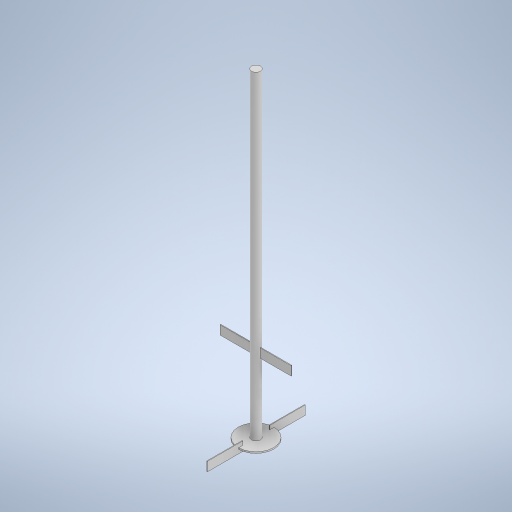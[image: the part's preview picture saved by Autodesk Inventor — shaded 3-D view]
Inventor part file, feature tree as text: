
AUTODESK INVENTOR PART (.ipt)
format: ipt  version: 2024 (Build 280153000, 153)  size: 284,160 bytes
history: native  units: mm
features: extrude x4, sketch x4
ambient origin geometry x8: Origin, YZ Plane, XZ Plane, XY Plane, X Axis, Y Axis, Z Axis, Center Point
bodies: Solid1 (feature_tree)
feature tree (8):
  extrude  "Extrusion1"  Depth=900.0mm TaperAngle=0.0deg
  extrude  "Extrusion2"  Depth=4.0mm TaperAngle=0.0deg
  extrude  "Extrusion3"  Depth=100.0mm
  extrude  "Extrusion4"  Depth=10.7mm
  sketch  "Sketch1"  dims[d0=25.4mm d1=900.0mm d2=0.0mm]
  sketch  "Sketch2"  dims[d3=100.0mm d4=4.0mm d5=0.0mm]
  sketch  "Sketch3"  dims[d6=100.0mm d7=25.0mm]
  sketch  "Sketch4"  dims[d8=25.4mm d9=10.7mm d10=2.0mm d11=0.0mm d12=25.4mm d13=200.0mm d14=87.3mm d15=87.3mm d16=200.0mm d17=2.0mm d18=0.0mm]
